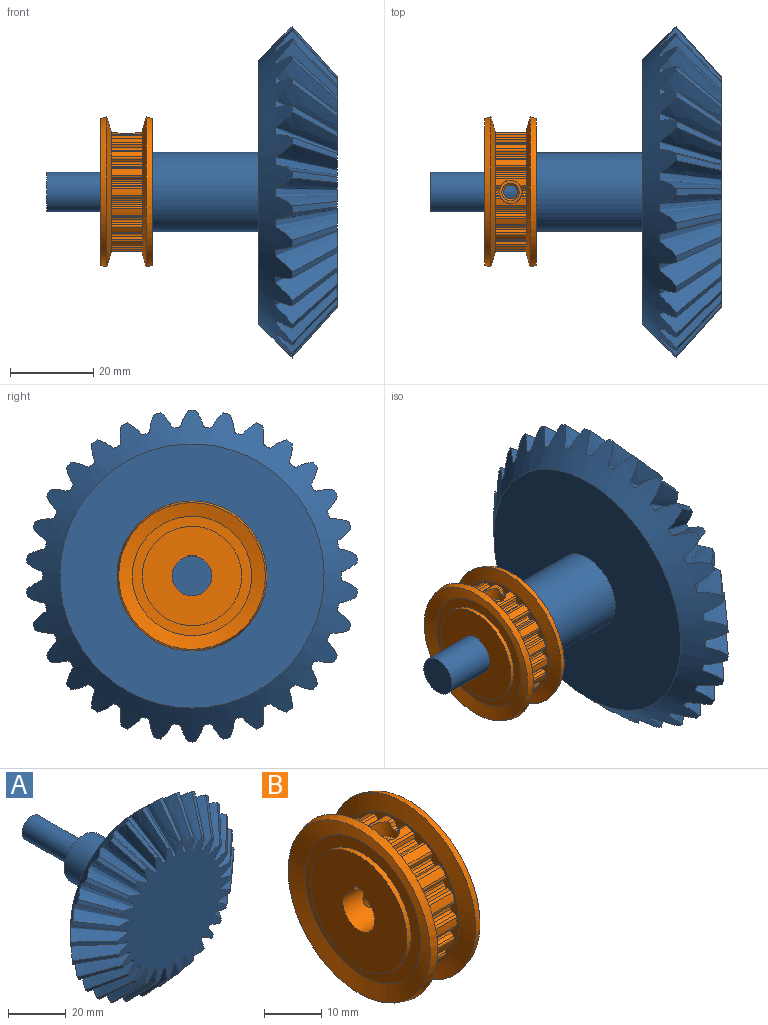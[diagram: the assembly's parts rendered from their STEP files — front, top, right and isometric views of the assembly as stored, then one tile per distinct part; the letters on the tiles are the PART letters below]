
ASSEMBLY  parts=2 mates=1
PART A: 67 faces, bbox 88.7x102.3x88.3 mm
  f0: cone r=31.75mm half-angle=45deg, axis (0,-1,0), area 2008mm2, adj f1,f2,f3,f4,f5,f6,f7,f8
  f1: cone r=39.9mm half-angle=48.2deg, axis (0,1,0), area 24.4mm2, adj f0,f32,f55,f56
  f2: plane 63.5x63.5mm, normal (0,1,0), area 2881.9mm2, adj f0,f63
  f3: cone r=39.9mm half-angle=48.2deg, axis (0,1,0), area 24.4mm2, adj f0,f32,f61,f62
  f4: cone r=39.9mm half-angle=48.2deg, axis (0,1,0), area 24.4mm2, adj f0,f32,f60,f61
  f5: cone r=39.9mm half-angle=48.2deg, axis (0,1,0), area 24.4mm2, adj f0,f32,f59,f60
  f6: cone r=39.9mm half-angle=48.2deg, axis (0,1,0), area 24.4mm2, adj f0,f32,f58,f59
  f7: cone r=39.9mm half-angle=48.2deg, axis (0,1,0), area 24.4mm2, adj f0,f32,f57,f58
  f8: cone r=39.9mm half-angle=48.2deg, axis (0,1,0), area 24.4mm2, adj f0,f32,f56,f57
  f9: cone r=39.9mm half-angle=48.2deg, axis (0,1,0), area 24.4mm2, adj f0,f32,f54,f55
  f10: cone r=39.9mm half-angle=48.2deg, axis (0,1,0), area 24.4mm2, adj f0,f32,f53,f54
  f11: cone r=39.9mm half-angle=48.2deg, axis (0,1,0), area 24.4mm2, adj f0,f32,f52,f53
  f12: cone r=39.9mm half-angle=48.2deg, axis (0,1,0), area 24.4mm2, adj f0,f32,f51,f52
  f13: cone r=39.9mm half-angle=48.2deg, axis (0,1,0), area 24.4mm2, adj f0,f32,f50,f51
  f14: cone r=39.9mm half-angle=48.2deg, axis (0,1,0), area 24.4mm2, adj f0,f32,f49,f50
  f15: cone r=39.9mm half-angle=48.2deg, axis (0,1,0), area 24.4mm2, adj f0,f32,f48,f49
  f16: cone r=39.9mm half-angle=48.2deg, axis (0,1,0), area 24.4mm2, adj f0,f32,f47,f48
  f17: cone r=39.9mm half-angle=48.2deg, axis (0,1,0), area 24.4mm2, adj f0,f32,f46,f47
  f18: cone r=39.9mm half-angle=48.2deg, axis (0,1,0), area 24.4mm2, adj f0,f32,f45,f46
  f19: cone r=39.9mm half-angle=48.2deg, axis (0,1,0), area 24.4mm2, adj f0,f32,f44,f45
  f20: cone r=39.9mm half-angle=48.2deg, axis (0,1,0), area 24.4mm2, adj f0,f32,f43,f44
  f21: cone r=39.9mm half-angle=48.2deg, axis (0,1,0), area 24.4mm2, adj f0,f32,f42,f43
  f22: cone r=39.9mm half-angle=48.2deg, axis (0,1,0), area 24.4mm2, adj f0,f32,f41,f42
  f23: cone r=39.9mm half-angle=48.2deg, axis (0,1,0), area 24.4mm2, adj f0,f32,f40,f41
  f24: cone r=39.9mm half-angle=48.2deg, axis (0,1,0), area 24.4mm2, adj f0,f32,f39,f40
  f25: cone r=39.9mm half-angle=48.2deg, axis (0,1,0), area 24.4mm2, adj f0,f32,f38,f39
  f26: cone r=39.9mm half-angle=48.2deg, axis (0,1,0), area 24.4mm2, adj f0,f32,f37,f38
  f27: cone r=39.9mm half-angle=48.2deg, axis (0,1,0), area 24.4mm2, adj f0,f32,f36,f37
  f28: cone r=39.9mm half-angle=48.2deg, axis (0,1,0), area 24.4mm2, adj f0,f32,f35,f36
  f29: cone r=39.9mm half-angle=48.2deg, axis (0,1,0), area 24.4mm2, adj f0,f32,f34,f35
  f30: cone r=39.9mm half-angle=48.2deg, axis (0,1,0), area 24.4mm2, adj f0,f32,f33,f34
  f31: cone r=39.9mm half-angle=48.2deg, axis (0,1,0), area 24.4mm2, adj f0,f32,f33,f62
  f32: plane 62.58x62.4mm, normal (0,-1,0), area 2024.1mm2, adj f1,f3,f4,f5,f6,f7,f8,f9
  f33: bspline ~40.65x40.27mm, area 204.9mm2, adj f0,f30,f31,f32
  f34: bspline ~40.63x40.27mm, area 204.9mm2, adj f0,f29,f30,f32
  f35: bspline ~40.27x38.83mm, area 204.9mm2, adj f0,f28,f29,f32
  f36: bspline ~40.27x35.34mm, area 186.9mm2, adj f0,f27,f28,f32
  f37: bspline ~40.27x33.01mm, area 186.9mm2, adj f0,f26,f27,f32
  f38: bspline ~40.27x37.29mm, area 204.9mm2, adj f0,f25,f26,f32
  f39: bspline ~40.27x39.95mm, area 204.8mm2, adj f0,f24,f25,f32
  f40: bspline ~40.86x40.27mm, area 204.8mm2, adj f0,f23,f24,f32
  f41: bspline ~40.86x40.27mm, area 204.8mm2, adj f0,f22,f23,f32
  f42: bspline ~40.27x39.95mm, area 204.9mm2, adj f0,f21,f22,f32
  f43: bspline ~40.27x37.29mm, area 204.9mm2, adj f0,f20,f21,f32
  f44: bspline ~40.27x33.01mm, area 186.9mm2, adj f0,f19,f20,f32
  f45: bspline ~40.27x35.34mm, area 186.9mm2, adj f0,f18,f19,f32
  f46: bspline ~40.27x38.83mm, area 204.9mm2, adj f0,f17,f18,f32
  f47: bspline ~40.63x40.27mm, area 204.9mm2, adj f0,f16,f17,f32
  f48: bspline ~40.65x40.27mm, area 204.8mm2, adj f0,f15,f16,f32
  f49: bspline ~40.63x40.27mm, area 204.9mm2, adj f0,f14,f15,f32
  f50: bspline ~40.27x38.83mm, area 204.9mm2, adj f0,f13,f14,f32
  f51: bspline ~40.27x35.34mm, area 186.9mm2, adj f0,f12,f13,f32
  f52: bspline ~40.27x33.01mm, area 186.9mm2, adj f0,f11,f12,f32
  f53: bspline ~40.27x37.29mm, area 204.9mm2, adj f0,f10,f11,f32
  f54: bspline ~40.27x39.95mm, area 204.8mm2, adj f0,f9,f10,f32
  f55: bspline ~40.86x40.27mm, area 204.8mm2, adj f0,f1,f9,f32
  f56: bspline ~40.86x40.27mm, area 204.8mm2, adj f0,f1,f8,f32
  f57: bspline ~40.27x39.95mm, area 204.9mm2, adj f0,f7,f8,f32
  f58: bspline ~40.27x37.29mm, area 204.9mm2, adj f0,f6,f7,f32
  f59: bspline ~40.27x33.01mm, area 186.9mm2, adj f0,f5,f6,f32
  f60: bspline ~40.27x35.34mm, area 186.9mm2, adj f0,f4,f5,f32
  f61: bspline ~40.27x38.83mm, area 204.9mm2, adj f0,f3,f4,f32
  f62: bspline ~40.63x40.27mm, area 204.8mm2, adj f0,f3,f31,f32
  f63: cylinder r=9.53mm len=25.39mm, axis (0,-1,0), area 1519.7mm2, adj f2,f64
  f64: plane 19.05x19.05mm, normal (0,1,0), area 213.8mm2, adj f63,f65
  f65: cylinder r=4.76mm len=25.4mm, axis (0,-1,0), area 760.1mm2, adj f64,f66
  f66: plane 9.53x9.53mm, normal (0,1,0), area 71.3mm2, adj f65
PART B: 187 faces, bbox 12.5x36.1x36.1 mm
  f0: cylinder r=3.97mm len=12.5mm, axis (-1,0,0), area 271.2mm2, adj f1,f2,f3,f9,f23,f168,f169,f170
  f1: plane 23.88x23.88mm, normal (-1,0,0), area 395.7mm2, adj f0,f25,f169,f170,f171
  f2: plane 23.88x23.88mm, normal (1,0,0), area 395.7mm2, adj f0,f3,f4,f168,f186
  f3: plane 5.11x1.19mm, normal (0,-1,0), area 6.1mm2, adj f0,f2,f4,f9
  f4: plane 5.11x2.39mm, normal (0,0,-1), area 11.4mm2, adj f2,f3,f9,f168
  f5: cylinder r=0.51mm len=1.46mm, axis (1,0,0), area 0.8mm2, adj f6,f22,f29,f48
  f6: cylinder r=2.78mm len=6.37mm, axis (0,0.87,-0.5), area 48.7mm2, adj f5,f7,f10,f11,f12,f13,f14,f15
  f7: plane 5.55x4.81mm, normal (0,0.87,-0.5), area 10.6mm2, adj f6,f24
  f8: cone r=2.08mm half-angle=45deg, axis (0,0,1), area 7.2mm2, adj f9,f28
  f9: cylinder r=1.65mm len=7.06mm, axis (0,0,1), area 65.2mm2, adj f0,f3,f4,f8,f25,f168,f169,f170
  f10: cylinder r=0.51mm len=1.46mm, axis (1,0,0), area 0.8mm2, adj f6,f12,f13,f29
  f11: cylinder r=0.51mm len=1.54mm, axis (1,0,0), area 0.9mm2, adj f6,f12,f14,f30
  f12: cylinder r=14.3mm len=7.49mm, axis (1,0,0), area 9.2mm2, adj f6,f10,f11,f29,f30,f47
  f13: plane 1.17x0.8mm, normal (0,-0.09,-1), area 0.9mm2, adj f6,f10,f15,f29
  f14: plane 1.25x0.8mm, normal (0,-0.09,-1), area 0.9mm2, adj f6,f11,f16,f30
  f15: cylinder r=0.51mm len=1.04mm, axis (1,0,0), area 0.6mm2, adj f6,f13,f17,f29
  f16: cylinder r=0.51mm len=1.12mm, axis (1,0,0), area 0.6mm2, adj f6,f14,f18,f30
  f17: cylinder r=12.9mm len=0.95mm, axis (1,0,0), area 0.6mm2, adj f6,f15,f19,f29
  f18: cylinder r=12.9mm len=1.02mm, axis (1,0,0), area 0.6mm2, adj f6,f16,f20,f30
  f19: cylinder r=0.51mm len=1.04mm, axis (1,0,0), area 0.6mm2, adj f6,f17,f22,f29
  f20: cylinder r=0.51mm len=1.12mm, axis (1,0,0), area 0.6mm2, adj f6,f18,f21,f30
  f21: plane 1.25x0.66mm, normal (0,0.82,0.57), area 0.9mm2, adj f6,f20,f30,f135
  f22: plane 1.17x0.66mm, normal (0,0.82,0.57), area 0.9mm2, adj f5,f6,f19,f29
  f23: cylinder r=1.65mm len=7.76mm, axis (0,0.87,-0.5), area 73.2mm2, adj f0,f24
  f24: cone r=2.08mm half-angle=45deg, axis (0,0.87,-0.5), area 7.2mm2, adj f7,f23
  f25: plane 5.11x2.39mm, normal (0,0,-1), area 11.4mm2, adj f1,f9,f169,f170
  f26: cylinder r=14.3mm len=7.49mm, axis (1,0,0), area 10.3mm2, adj f27,f29,f30,f44,f45,f167
  f27: cylinder r=2.78mm len=5.55mm, axis (0,0,1), area 48.7mm2, adj f26,f28,f31,f32,f33,f34,f35,f36
  f28: plane 5.55x5.55mm, normal (0,0,1), area 10.6mm2, adj f8,f27
  f29: plane 29.11x29.11mm, normal (1,0,0), area 71.1mm2, adj f5,f10,f12,f13,f15,f17,f19,f22
  f30: plane 29.64x29.64mm, normal (-1,0,0), area 95.6mm2, adj f11,f12,f14,f16,f18,f20,f21,f26
  f31: cylinder r=0.51mm len=1.46mm, axis (1,0,0), area 0.8mm2, adj f27,f29,f33,f34
  f32: cylinder r=0.51mm len=1.54mm, axis (1,0,0), area 0.9mm2, adj f27,f30,f33,f35
  f33: cylinder r=14.3mm len=7.49mm, axis (1,0,0), area 9.2mm2, adj f27,f29,f30,f31,f32,f134
  f34: plane 1.17x0.73mm, normal (0,0.91,0.42), area 0.9mm2, adj f27,f29,f31,f36
  f35: plane 1.25x0.73mm, normal (0,0.91,0.42), area 0.9mm2, adj f27,f30,f32,f37
  f36: cylinder r=0.51mm len=1.04mm, axis (1,0,0), area 0.6mm2, adj f27,f29,f34,f38
  f37: cylinder r=0.51mm len=1.12mm, axis (1,0,0), area 0.6mm2, adj f27,f30,f35,f39
  f38: cylinder r=12.9mm len=0.95mm, axis (1,0,0), area 0.6mm2, adj f27,f29,f36,f40
  f39: cylinder r=12.9mm len=1.02mm, axis (1,0,0), area 0.6mm2, adj f27,f30,f37,f41
  f40: cylinder r=0.51mm len=1.04mm, axis (1,0,0), area 0.6mm2, adj f27,f29,f38,f43
  f41: cylinder r=0.51mm len=1.12mm, axis (1,0,0), area 0.6mm2, adj f27,f30,f39,f42
  f42: plane 1.25x0.73mm, normal (0,-0.91,0.42), area 0.9mm2, adj f27,f30,f41,f45
  f43: plane 1.17x0.73mm, normal (0,-0.91,0.42), area 0.9mm2, adj f27,f29,f40,f44
  f44: cylinder r=0.51mm len=1.46mm, axis (1,0,0), area 0.8mm2, adj f26,f27,f29,f43
  f45: cylinder r=0.51mm len=1.54mm, axis (1,0,0), area 0.9mm2, adj f26,f27,f30,f42
  f46: plane 7.49x0.65mm, normal (0,0.57,0.82), area 6mm2, adj f29,f30,f47,f182
  f47: cylinder r=0.51mm len=7.49mm, axis (1,0,0), area 4.8mm2, adj f12,f29,f30,f46
  f48: cylinder r=14.3mm len=7.49mm, axis (1,0,0), area 10.3mm2, adj f5,f6,f29,f30,f49,f135
  f49: cylinder r=0.51mm len=7.49mm, axis (1,0,0), area 4.8mm2, adj f29,f30,f48,f50
  f50: plane 7.49x0.72mm, normal (0,-0.42,-0.91), area 6mm2, adj f29,f30,f49,f51
  f51: cylinder r=0.51mm len=7.49mm, axis (1,0,0), area 4.4mm2, adj f29,f30,f50,f52
  f52: cylinder r=12.9mm len=7.49mm, axis (1,0,0), area 4.6mm2, adj f29,f30,f51,f53
  f53: cylinder r=0.51mm len=7.49mm, axis (1,0,0), area 4.4mm2, adj f29,f30,f52,f54
  f54: plane 7.49x0.77mm, normal (0,0.97,0.26), area 6mm2, adj f29,f30,f53,f55
  f55: cylinder r=0.51mm len=7.49mm, axis (1,0,0), area 4.8mm2, adj f29,f30,f54,f56
  f56: cylinder r=14.3mm len=7.49mm, axis (1,0,0), area 12.9mm2, adj f29,f30,f55,f57
  f57: cylinder r=0.51mm len=7.49mm, axis (1,0,0), area 4.8mm2, adj f29,f30,f56,f58
  f58: plane 7.49x0.56mm, normal (0,-0.71,-0.71), area 6mm2, adj f29,f30,f57,f59
  f59: cylinder r=0.51mm len=7.49mm, axis (1,0,0), area 4.4mm2, adj f29,f30,f58,f60
  f60: cylinder r=12.9mm len=7.49mm, axis (1,0,0), area 4.6mm2, adj f29,f30,f59,f61
  f61: cylinder r=0.51mm len=7.49mm, axis (1,0,0), area 4.4mm2, adj f29,f30,f60,f62
  f62: plane 7.49x0.8mm, normal (0,1,-0.09), area 6mm2, adj f29,f30,f61,f63
  f63: cylinder r=0.51mm len=7.49mm, axis (1,0,0), area 4.8mm2, adj f29,f30,f62,f64
  f64: cylinder r=14.3mm len=7.49mm, axis (1,0,0), area 12.9mm2, adj f29,f30,f63,f65
  f65: cylinder r=0.51mm len=7.49mm, axis (1,0,0), area 4.8mm2, adj f29,f30,f64,f66
  f66: plane 7.49x0.72mm, normal (0,-0.91,-0.42), area 6mm2, adj f29,f30,f65,f67
  f67: cylinder r=0.51mm len=7.49mm, axis (1,0,0), area 4.4mm2, adj f29,f30,f66,f68
  f68: cylinder r=12.9mm len=7.49mm, axis (1,0,0), area 4.6mm2, adj f29,f30,f67,f69
  f69: cylinder r=0.51mm len=7.49mm, axis (1,0,0), area 4.4mm2, adj f29,f30,f68,f70
  f70: plane 7.49x0.72mm, normal (0,0.91,-0.42), area 6mm2, adj f29,f30,f69,f71
  f71: cylinder r=0.51mm len=7.49mm, axis (1,0,0), area 4.8mm2, adj f29,f30,f70,f72
  f72: cylinder r=14.3mm len=7.49mm, axis (1,0,0), area 12.9mm2, adj f29,f30,f71,f73
  f73: cylinder r=0.51mm len=7.49mm, axis (1,0,0), area 4.8mm2, adj f29,f30,f72,f74
  f74: plane 7.49x0.8mm, normal (0,-1,-0.09), area 6mm2, adj f29,f30,f73,f75
  f75: cylinder r=0.51mm len=7.49mm, axis (1,0,0), area 4.4mm2, adj f29,f30,f74,f76
  f76: cylinder r=12.9mm len=7.49mm, axis (1,0,0), area 4.6mm2, adj f29,f30,f75,f77
  f77: cylinder r=0.51mm len=7.49mm, axis (1,0,0), area 4.4mm2, adj f29,f30,f76,f78
  f78: plane 7.49x0.56mm, normal (0,0.71,-0.71), area 6mm2, adj f29,f30,f77,f79
  f79: cylinder r=0.51mm len=7.49mm, axis (1,0,0), area 4.8mm2, adj f29,f30,f78,f80
  f80: cylinder r=14.3mm len=7.49mm, axis (1,0,0), area 12.9mm2, adj f29,f30,f79,f81
  f81: cylinder r=0.51mm len=7.49mm, axis (1,0,0), area 4.8mm2, adj f29,f30,f80,f82
  f82: plane 7.49x0.77mm, normal (0,-0.97,0.26), area 6mm2, adj f29,f30,f81,f83
  f83: cylinder r=0.51mm len=7.49mm, axis (1,0,0), area 4.4mm2, adj f29,f30,f82,f84
  f84: cylinder r=12.9mm len=7.49mm, axis (1,0,0), area 4.6mm2, adj f29,f30,f83,f85
  f85: cylinder r=0.51mm len=7.49mm, axis (1,0,0), area 4.4mm2, adj f29,f30,f84,f86
  f86: plane 7.49x0.72mm, normal (0,0.42,-0.91), area 6mm2, adj f29,f30,f85,f87
  f87: cylinder r=0.51mm len=7.49mm, axis (1,0,0), area 4.8mm2, adj f29,f30,f86,f88
  f88: cylinder r=14.3mm len=7.49mm, axis (1,0,0), area 12.9mm2, adj f29,f30,f87,f89
  f89: cylinder r=0.51mm len=7.49mm, axis (1,0,0), area 4.8mm2, adj f29,f30,f88,f90
  f90: plane 7.49x0.65mm, normal (0,-0.82,0.57), area 6mm2, adj f29,f30,f89,f91
  f91: cylinder r=0.51mm len=7.49mm, axis (1,0,0), area 4.4mm2, adj f29,f30,f90,f92
  f92: cylinder r=12.9mm len=7.49mm, axis (1,0,0), area 4.6mm2, adj f29,f30,f91,f93
  f93: cylinder r=0.51mm len=7.49mm, axis (1,0,0), area 4.4mm2, adj f29,f30,f92,f94
  f94: plane 7.49x0.8mm, normal (0,0.09,-1), area 6mm2, adj f29,f30,f93,f95
  f95: cylinder r=0.51mm len=7.49mm, axis (1,0,0), area 4.8mm2, adj f29,f30,f94,f96
  f96: cylinder r=14.3mm len=7.49mm, axis (1,0,0), area 12.9mm2, adj f29,f30,f95,f97
  f97: cylinder r=0.51mm len=7.49mm, axis (1,0,0), area 4.8mm2, adj f29,f30,f96,f98
  f98: plane 7.49x0.65mm, normal (0,-0.57,0.82), area 6mm2, adj f29,f30,f97,f99
  f99: cylinder r=0.51mm len=7.49mm, axis (1,0,0), area 4.4mm2, adj f29,f30,f98,f100
  f100: cylinder r=12.9mm len=7.49mm, axis (1,0,0), area 4.6mm2, adj f29,f30,f99,f101
  f101: cylinder r=0.51mm len=7.49mm, axis (1,0,0), area 4.4mm2, adj f29,f30,f100,f102
  f102: plane 7.49x0.77mm, normal (0,-0.26,-0.97), area 6mm2, adj f29,f30,f101,f103
  f103: cylinder r=0.51mm len=7.49mm, axis (1,0,0), area 4.8mm2, adj f29,f30,f102,f104
  f104: cylinder r=14.3mm len=7.49mm, axis (1,0,0), area 12.9mm2, adj f29,f30,f103,f105
  f105: cylinder r=0.51mm len=7.49mm, axis (1,0,0), area 4.8mm2, adj f29,f30,f104,f106
  f106: plane 7.49x0.77mm, normal (0,-0.26,0.97), area 6mm2, adj f29,f30,f105,f107
  f107: cylinder r=0.51mm len=7.49mm, axis (1,0,0), area 4.4mm2, adj f29,f30,f106,f108
  f108: cylinder r=12.9mm len=7.49mm, axis (1,0,0), area 4.6mm2, adj f29,f30,f107,f109
  f109: cylinder r=0.51mm len=7.49mm, axis (1,0,0), area 4.4mm2, adj f29,f30,f108,f110
  f110: plane 7.49x0.65mm, normal (0,-0.57,-0.82), area 6mm2, adj f29,f30,f109,f111
  f111: cylinder r=0.51mm len=7.49mm, axis (1,0,0), area 4.8mm2, adj f29,f30,f110,f112
  f112: cylinder r=14.3mm len=7.49mm, axis (1,0,0), area 12.9mm2, adj f29,f30,f111,f113
  f113: cylinder r=0.51mm len=7.49mm, axis (1,0,0), area 4.8mm2, adj f29,f30,f112,f114
  f114: plane 7.49x0.8mm, normal (0,0.09,1), area 6mm2, adj f29,f30,f113,f177
  f115: cylinder r=12.9mm len=7.49mm, axis (1,0,0), area 4.6mm2, adj f29,f30,f116,f177
  f116: cylinder r=0.51mm len=7.49mm, axis (1,0,0), area 4.4mm2, adj f29,f30,f115,f117
  f117: plane 7.49x0.65mm, normal (0,-0.82,-0.57), area 6mm2, adj f29,f30,f116,f118
  f118: cylinder r=0.51mm len=7.49mm, axis (1,0,0), area 4.8mm2, adj f29,f30,f117,f119
  f119: cylinder r=14.3mm len=7.49mm, axis (1,0,0), area 12.9mm2, adj f29,f30,f118,f120
  f120: cylinder r=0.51mm len=7.49mm, axis (1,0,0), area 4.8mm2, adj f29,f30,f119,f121
  f121: plane 7.49x0.72mm, normal (0,0.42,0.91), area 6mm2, adj f29,f30,f120,f122
  f122: cylinder r=0.51mm len=7.49mm, axis (1,0,0), area 4.4mm2, adj f29,f30,f121,f123
  f123: cylinder r=12.9mm len=7.49mm, axis (1,0,0), area 4.6mm2, adj f29,f30,f122,f124
  f124: cylinder r=0.51mm len=7.49mm, axis (1,0,0), area 4.4mm2, adj f29,f30,f123,f125
  f125: plane 7.49x0.77mm, normal (0,-0.97,-0.26), area 6mm2, adj f29,f30,f124,f126
  f126: cylinder r=0.51mm len=7.49mm, axis (1,0,0), area 4.8mm2, adj f29,f30,f125,f127
  f127: cylinder r=14.3mm len=7.49mm, axis (1,0,0), area 12.9mm2, adj f29,f30,f126,f128
  f128: cylinder r=0.51mm len=7.49mm, axis (1,0,0), area 4.8mm2, adj f29,f30,f127,f129
  f129: plane 7.49x0.56mm, normal (0,0.71,0.71), area 6mm2, adj f29,f30,f128,f130
  f130: cylinder r=0.51mm len=7.49mm, axis (1,0,0), area 4.4mm2, adj f29,f30,f129,f131
  f131: cylinder r=12.9mm len=7.49mm, axis (1,0,0), area 4.6mm2, adj f29,f30,f130,f132
  f132: cylinder r=0.51mm len=7.49mm, axis (1,0,0), area 4.4mm2, adj f29,f30,f131,f133
  f133: plane 7.49x0.8mm, normal (0,-1,0.09), area 6mm2, adj f29,f30,f132,f134
  f134: cylinder r=0.51mm len=7.49mm, axis (1,0,0), area 4.8mm2, adj f29,f30,f33,f133
  f135: cylinder r=0.51mm len=1.54mm, axis (1,0,0), area 0.9mm2, adj f6,f21,f30,f48
  f136: cylinder r=12.9mm len=7.49mm, axis (1,0,0), area 4.6mm2, adj f29,f30,f137,f182
  f137: cylinder r=0.51mm len=7.49mm, axis (1,0,0), area 4.4mm2, adj f29,f30,f136,f138
  f138: plane 7.49x0.77mm, normal (0,0.26,-0.97), area 6mm2, adj f29,f30,f137,f139
  f139: cylinder r=0.51mm len=7.49mm, axis (1,0,0), area 4.8mm2, adj f29,f30,f138,f140
  f140: cylinder r=14.3mm len=7.49mm, axis (1,0,0), area 12.9mm2, adj f29,f30,f139,f141
  f141: cylinder r=0.51mm len=7.49mm, axis (1,0,0), area 4.8mm2, adj f29,f30,f140,f142
  f142: plane 7.49x0.77mm, normal (0,0.26,0.97), area 6mm2, adj f29,f30,f141,f143
  f143: cylinder r=0.51mm len=7.49mm, axis (1,0,0), area 4.4mm2, adj f29,f30,f142,f144
  f144: cylinder r=12.9mm len=7.49mm, axis (1,0,0), area 4.6mm2, adj f29,f30,f143,f181
  f145: plane 7.49x0.65mm, normal (0,0.57,-0.82), area 6mm2, adj f29,f30,f146,f181
  f146: cylinder r=0.51mm len=7.49mm, axis (1,0,0), area 4.8mm2, adj f29,f30,f145,f147
  f147: cylinder r=14.3mm len=7.49mm, axis (1,0,0), area 12.9mm2, adj f29,f30,f146,f148
  f148: cylinder r=0.51mm len=7.49mm, axis (1,0,0), area 4.8mm2, adj f29,f30,f147,f149
  f149: plane 7.49x0.8mm, normal (0,-0.09,1), area 6mm2, adj f29,f30,f148,f180
  f150: cylinder r=12.9mm len=7.49mm, axis (1,0,0), area 4.6mm2, adj f29,f30,f151,f180
  f151: cylinder r=0.51mm len=7.49mm, axis (1,0,0), area 4.4mm2, adj f29,f30,f150,f152
  f152: plane 7.49x0.65mm, normal (0,0.82,-0.57), area 6mm2, adj f29,f30,f151,f153
  f153: cylinder r=0.51mm len=7.49mm, axis (1,0,0), area 4.8mm2, adj f29,f30,f152,f154
  f154: cylinder r=14.3mm len=7.49mm, axis (1,0,0), area 12.9mm2, adj f29,f30,f153,f155
  f155: cylinder r=0.51mm len=7.49mm, axis (1,0,0), area 4.8mm2, adj f29,f30,f154,f156
  f156: plane 7.49x0.72mm, normal (0,-0.42,0.91), area 6mm2, adj f29,f30,f155,f157
  f157: cylinder r=0.51mm len=7.49mm, axis (1,0,0), area 4.4mm2, adj f29,f30,f156,f158
  f158: cylinder r=12.9mm len=7.49mm, axis (1,0,0), area 4.6mm2, adj f29,f30,f157,f179
  f159: plane 7.49x0.77mm, normal (0,0.97,-0.26), area 6mm2, adj f29,f30,f160,f179
  f160: cylinder r=0.51mm len=7.49mm, axis (1,0,0), area 4.8mm2, adj f29,f30,f159,f161
  f161: cylinder r=14.3mm len=7.49mm, axis (1,0,0), area 12.9mm2, adj f29,f30,f160,f162
  f162: cylinder r=0.51mm len=7.49mm, axis (1,0,0), area 4.8mm2, adj f29,f30,f161,f163
  f163: plane 7.49x0.56mm, normal (0,-0.71,0.71), area 6mm2, adj f29,f30,f162,f178
  f164: cylinder r=12.9mm len=7.49mm, axis (1,0,0), area 4.6mm2, adj f29,f30,f165,f178
  f165: cylinder r=0.51mm len=7.49mm, axis (1,0,0), area 4.4mm2, adj f29,f30,f164,f166
  f166: plane 7.49x0.8mm, normal (0,1,0.09), area 6mm2, adj f29,f30,f165,f167
  f167: cylinder r=0.51mm len=7.49mm, axis (1,0,0), area 4.8mm2, adj f26,f29,f30,f166
  f168: plane 5.11x1.19mm, normal (0,1,0), area 6.1mm2, adj f0,f2,f4,f9
  f169: plane 5.11x1.19mm, normal (0,1,0), area 6.1mm2, adj f0,f1,f9,f25
  f170: plane 5.11x1.19mm, normal (0,-1,0), area 6.1mm2, adj f0,f1,f9,f25
  f171: cylinder r=11.94mm len=23.88mm, axis (-1,0,0), area 76.2mm2, adj f1,f172
  f172: plane 28.68x28.68mm, normal (-1,0,0), area 198.3mm2, adj f171,f173
  f173: cone r=17.61mm half-angle=74deg, axis (-1,0,0), area 341.9mm2, adj f172,f174
  f174: cone r=18.03mm half-angle=16deg, axis (1,0,0), area 170.7mm2, adj f173,f175
  f175: cone r=14.55mm half-angle=74deg, axis (-1,0,0), area 370.6mm2, adj f29,f174
  f176: cone r=18.03mm half-angle=74deg, axis (1,0,0), area 345.1mm2, adj f30,f183
  f177: cylinder r=0.51mm len=7.49mm, axis (1,0,0), area 4.4mm2, adj f29,f30,f114,f115
  f178: cylinder r=0.51mm len=7.49mm, axis (1,0,0), area 4.4mm2, adj f29,f30,f163,f164
  f179: cylinder r=0.51mm len=7.49mm, axis (1,0,0), area 4.4mm2, adj f29,f30,f158,f159
  f180: cylinder r=0.51mm len=7.49mm, axis (1,0,0), area 4.4mm2, adj f29,f30,f149,f150
  f181: cylinder r=0.51mm len=7.49mm, axis (1,0,0), area 4.4mm2, adj f29,f30,f144,f145
  f182: cylinder r=0.51mm len=7.49mm, axis (1,0,0), area 4.4mm2, adj f29,f30,f46,f136
  f183: cone r=17.61mm half-angle=16deg, axis (-1,0,0), area 170.7mm2, adj f176,f184
  f184: cone r=14.34mm half-angle=74deg, axis (1,0,0), area 341.9mm2, adj f183,f185
  f185: plane 28.68x28.68mm, normal (1,0,0), area 198.3mm2, adj f184,f186
  f186: cylinder r=11.94mm len=23.88mm, axis (-1,0,0), area 76.2mm2, adj f2,f185
PLACE A rot(axis=(-0.58,0.58,0.58),120deg) t=(82.34,0,0)mm
PLACE B at identity
MATE fastened A.f0 <-> B.f0  axis (1,0,0) through (12.5,0,0)mm
